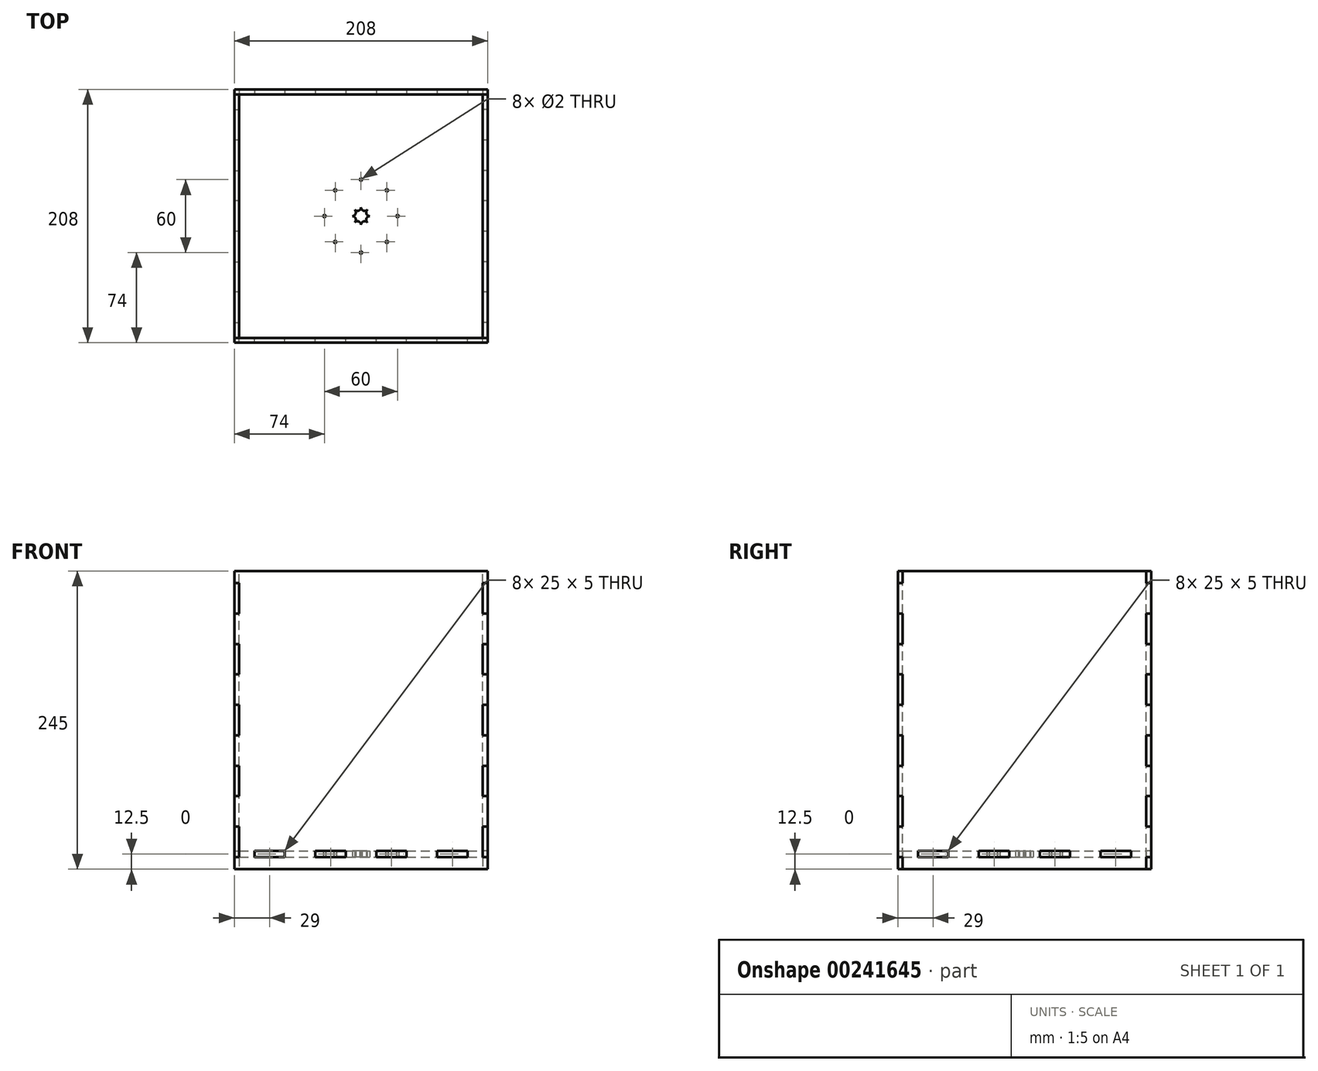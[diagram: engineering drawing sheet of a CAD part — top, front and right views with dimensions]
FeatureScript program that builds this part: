
annotation { "Feature Type Name" : "Feature", "Feature Type Description" : "" }
export const myFeature = defineFeature(function(context is Context, id is Id, definition is map)
    precondition{}
    {
        {
            var Q0;
            Q0=qCreatedBy(makeId("Top.planeOp"),FACE);
            var sketch = newSketch(context, id + "F0", { "sketchPlane" : qUnion([Q0])});
            skLineSegment(sketch, "E0.left", {"start": v(-100, -100) * mm, "end": v(-100, -100) * mm});
            skPoint(sketch, "E0.middle", {"position": v(0, 0) * mm});
            skLineSegment(sketch, "E1", {"start": v(-30, 0) * mm, "end": v(-30, 0) * mm});
            skLineSegment(sketch, "E2", {"start": v(0, -30) * mm, "end": v(0, -30) * mm});
            skLineSegment(sketch, "E3", {"start": v(-20.5, -20.5) * mm, "end": v(-5.12, -5.12) * mm});
            skArc(sketch, "E4.filletArc", {"start": v(0, -7.24) * mm, "mid": v(-1.85, -4.47) * mm, "end": v(-5.12, -5.12) * mm});
            skArc(sketch, "E5.filletArc", {"start": v(-5.12, -5.12) * mm, "mid": v(-4.47, -1.85) * mm, "end": v(-7.24, 0) * mm});
            skLineSegment(sketch, "E6", {"start": v(-29, 0) * mm, "end": v(-7.24, 0) * mm});
            skLineSegment(sketch, "E7", {"start": v(-5.12, 5.12) * mm, "end": v(-20.5, 20.5) * mm});
            skArc(sketch, "E8.filletArc", {"start": v(-7.24, 0) * mm, "mid": v(-4.47, 1.85) * mm, "end": v(-5.12, 5.12) * mm});
            skArc(sketch, "E9.filletArc", {"start": v(-5.12, 5.12) * mm, "mid": v(-1.85, 4.47) * mm, "end": v(0, 7.24) * mm});
            skLineSegment(sketch, "E10", {"start": v(7.24, 0) * mm, "end": v(29, 0) * mm});
            skLineSegment(sketch, "E11", {"start": v(0, -29) * mm, "end": v(0, -7.24) * mm});
            skLineSegment(sketch, "E12", {"start": v(0, 7.24) * mm, "end": v(0, 29) * mm});
            skLineSegment(sketch, "E13", {"start": v(0, 30) * mm, "end": v(0, 30) * mm});
            skLineSegment(sketch, "E14", {"start": v(30, 0) * mm, "end": v(30, 0) * mm});
            skLineSegment(sketch, "E15.trimOffspring", {"start": v(5.12, 5.12) * mm, "end": v(20.5, 20.5) * mm});
            skArc(sketch, "E16.filletArc", {"start": v(0, 7.24) * mm, "mid": v(1.85, 4.47) * mm, "end": v(5.12, 5.12) * mm});
            skArc(sketch, "E17.filletArc", {"start": v(5.12, 5.12) * mm, "mid": v(4.47, 1.85) * mm, "end": v(7.24, 0) * mm});
            skLineSegment(sketch, "E18.trimOffspring", {"start": v(5.12, -5.12) * mm, "end": v(20.5, -20.5) * mm});
            skArc(sketch, "E19.filletArc", {"start": v(5.12, -5.12) * mm, "mid": v(1.85, -4.47) * mm, "end": v(0, -7.24) * mm});
            skArc(sketch, "E20.filletArc", {"start": v(7.24, 0) * mm, "mid": v(4.47, -1.85) * mm, "end": v(5.12, -5.12) * mm});
            skCircle(sketch, "E21", {"center": v(-21.21, 21.21) * mm, "radius": 1 * mm});
            skCircle(sketch, "E22", {"center": v(-30, 0) * mm, "radius": 1 * mm});
            skCircle(sketch, "E23", {"center": v(-21.21, -21.21) * mm, "radius": 1 * mm});
            skCircle(sketch, "E24", {"center": v(0, -30) * mm, "radius": 1 * mm});
            skCircle(sketch, "E25", {"center": v(21.21, -21.21) * mm, "radius": 1 * mm});
            skCircle(sketch, "E26", {"center": v(30, 0) * mm, "radius": 1 * mm});
            skCircle(sketch, "E27", {"center": v(21.21, 21.21) * mm, "radius": 1 * mm});
            skCircle(sketch, "E28", {"center": v(0, 30) * mm, "radius": 1 * mm});
            skLineSegment(sketch, "E29", {"start": v(-100, -100) * mm, "end": v(-100, -87.5) * mm});
            skLineSegment(sketch, "E30", {"start": v(-100, 0) * mm, "end": v(-100, 12.5) * mm});
            skLineSegment(sketch, "E31", {"start": v(-100, 50) * mm, "end": v(-100, 62.5) * mm});
            skLineSegment(sketch, "E32", {"start": v(-100, -50) * mm, "end": v(-100, -37.5) * mm});
            skLineSegment(sketch, "E33", {"start": v(-100, -62.5) * mm, "end": v(-100, -50) * mm});
            skLineSegment(sketch, "E34", {"start": v(-100, -12.5) * mm, "end": v(-100, 0) * mm});
            skLineSegment(sketch, "E35", {"start": v(-100, 37.5) * mm, "end": v(-100, 50) * mm});
            skLineSegment(sketch, "E36", {"start": v(-100, 87.5) * mm, "end": v(-100, 100) * mm});
            skLineSegment(sketch, "E37", {"start": v(-100, 12.5) * mm, "end": v(-104, 12.5) * mm});
            skLineSegment(sketch, "E38", {"start": v(-104, 12.5) * mm, "end": v(-104, 37.5) * mm});
            skLineSegment(sketch, "E39", {"start": v(-104, 37.5) * mm, "end": v(-100, 37.5) * mm});
            skLineSegment(sketch, "E40", {"start": v(-100, -12.5) * mm, "end": v(-104, -12.5) * mm});
            skLineSegment(sketch, "E41", {"start": v(-104, -12.5) * mm, "end": v(-104, -37.5) * mm});
            skLineSegment(sketch, "E42", {"start": v(-104, -37.5) * mm, "end": v(-100, -37.5) * mm});
            skLineSegment(sketch, "E43", {"start": v(-100, -62.5) * mm, "end": v(-104, -62.5) * mm});
            skLineSegment(sketch, "E44", {"start": v(-104, -62.5) * mm, "end": v(-104, -87.5) * mm});
            skLineSegment(sketch, "E45", {"start": v(-104, -87.5) * mm, "end": v(-100, -87.5) * mm});
            skLineSegment(sketch, "E46", {"start": v(-100, 62.5) * mm, "end": v(-104, 62.5) * mm});
            skLineSegment(sketch, "E47", {"start": v(-104, 62.5) * mm, "end": v(-104, 87.5) * mm});
            skLineSegment(sketch, "E48", {"start": v(-104, 87.5) * mm, "end": v(-100, 87.5) * mm});
            skLineSegment(sketch, "E49.MirrorCS", {"start": v(100, -62.5) * mm, "end": v(104, -62.5) * mm});
            skLineSegment(sketch, "E50.MirrorCS", {"start": v(104, -87.5) * mm, "end": v(100, -87.5) * mm});
            skLineSegment(sketch, "E51.MirrorCS", {"start": v(104, -37.5) * mm, "end": v(100, -37.5) * mm});
            skLineSegment(sketch, "E52.MirrorCS", {"start": v(104, -62.5) * mm, "end": v(104, -87.5) * mm});
            skLineSegment(sketch, "E53.MirrorCS", {"start": v(104, -12.5) * mm, "end": v(104, -37.5) * mm});
            skLineSegment(sketch, "E54.MirrorCS", {"start": v(100, -100) * mm, "end": v(100, -87.5) * mm});
            skLineSegment(sketch, "E55.MirrorCS", {"start": v(100, -50) * mm, "end": v(100, -37.5) * mm});
            skLineSegment(sketch, "E56.MirrorCS", {"start": v(100, -62.5) * mm, "end": v(100, -50) * mm});
            skLineSegment(sketch, "E57.MirrorCS", {"start": v(100, -12.5) * mm, "end": v(104, -12.5) * mm});
            skLineSegment(sketch, "E58.MirrorCS", {"start": v(100, 12.5) * mm, "end": v(104, 12.5) * mm});
            skLineSegment(sketch, "E59.MirrorCS", {"start": v(104, 37.5) * mm, "end": v(100, 37.5) * mm});
            skLineSegment(sketch, "E60.MirrorCS", {"start": v(100, 62.5) * mm, "end": v(104, 62.5) * mm});
            skLineSegment(sketch, "E61.MirrorCS", {"start": v(104, 87.5) * mm, "end": v(100, 87.5) * mm});
            skLineSegment(sketch, "E62.MirrorCS", {"start": v(100, 87.5) * mm, "end": v(100, 100) * mm});
            skLineSegment(sketch, "E63.MirrorCS", {"start": v(100, 37.5) * mm, "end": v(100, 50) * mm});
            skLineSegment(sketch, "E64.MirrorCS", {"start": v(104, 12.5) * mm, "end": v(104, 37.5) * mm});
            skLineSegment(sketch, "E65.MirrorCS", {"start": v(100, -12.5) * mm, "end": v(100, 0) * mm});
            skLineSegment(sketch, "E66.MirrorCS", {"start": v(104, 62.5) * mm, "end": v(104, 87.5) * mm});
            skLineSegment(sketch, "E67.MirrorCS", {"start": v(100, 0) * mm, "end": v(100, 12.5) * mm});
            skLineSegment(sketch, "E68.MirrorCS", {"start": v(100, 50) * mm, "end": v(100, 62.5) * mm});
            skLineSegment(sketch, "E69.MirrorCS", {"start": v(-62.5, -100) * mm, "end": v(-62.5, -104) * mm});
            skLineSegment(sketch, "E70.MirrorCS", {"start": v(-87.5, -104) * mm, "end": v(-87.5, -100) * mm});
            skLineSegment(sketch, "E71.MirrorCS", {"start": v(-12.5, -100) * mm, "end": v(-12.5, -104) * mm});
            skLineSegment(sketch, "E72.MirrorCS", {"start": v(12.5, -100) * mm, "end": v(12.5, -104) * mm});
            skLineSegment(sketch, "E73.MirrorCS", {"start": v(62.5, -100) * mm, "end": v(62.5, -104) * mm});
            skLineSegment(sketch, "E74.MirrorCS", {"start": v(37.5, -104) * mm, "end": v(37.5, -100) * mm});
            skLineSegment(sketch, "E75.MirrorCS", {"start": v(-37.5, -104) * mm, "end": v(-37.5, -100) * mm});
            skLineSegment(sketch, "E76.MirrorCS", {"start": v(87.5, -104) * mm, "end": v(87.5, -100) * mm});
            skLineSegment(sketch, "E77.MirrorCS", {"start": v(-62.5, -104) * mm, "end": v(-87.5, -104) * mm});
            skLineSegment(sketch, "E78.MirrorCS", {"start": v(87.5, -100) * mm, "end": v(100, -100) * mm});
            skLineSegment(sketch, "E79.MirrorCS", {"start": v(37.5, -100) * mm, "end": v(50, -100) * mm});
            skLineSegment(sketch, "E80.MirrorCS", {"start": v(-50, -100) * mm, "end": v(-37.5, -100) * mm});
            skLineSegment(sketch, "E81.MirrorCS", {"start": v(-62.5, -100) * mm, "end": v(-50, -100) * mm});
            skLineSegment(sketch, "E82.MirrorCS", {"start": v(-100, -100) * mm, "end": v(-87.5, -100) * mm});
            skLineSegment(sketch, "E83.MirrorCS", {"start": v(12.5, -104) * mm, "end": v(37.5, -104) * mm});
            skLineSegment(sketch, "E84.MirrorCS", {"start": v(0, -100) * mm, "end": v(12.5, -100) * mm});
            skLineSegment(sketch, "E85.MirrorCS", {"start": v(50, -100) * mm, "end": v(62.5, -100) * mm});
            skLineSegment(sketch, "E86.MirrorCS", {"start": v(-12.5, -104) * mm, "end": v(-37.5, -104) * mm});
            skLineSegment(sketch, "E87.MirrorCS", {"start": v(-12.5, -100) * mm, "end": v(0, -100) * mm});
            skLineSegment(sketch, "E88.MirrorCS", {"start": v(62.5, -104) * mm, "end": v(87.5, -104) * mm});
            skLineSegment(sketch, "E89.MirrorCS", {"start": v(62.5, 100) * mm, "end": v(62.5, 104) * mm});
            skLineSegment(sketch, "E90.MirrorCS", {"start": v(37.5, 104) * mm, "end": v(37.5, 100) * mm});
            skLineSegment(sketch, "E91.MirrorCS", {"start": v(-37.5, 104) * mm, "end": v(-37.5, 100) * mm});
            skLineSegment(sketch, "E92.MirrorCS", {"start": v(87.5, 104) * mm, "end": v(87.5, 100) * mm});
            skLineSegment(sketch, "E93.MirrorCS", {"start": v(-12.5, 100) * mm, "end": v(-12.5, 104) * mm});
            skLineSegment(sketch, "E94.MirrorCS", {"start": v(-87.5, 104) * mm, "end": v(-87.5, 100) * mm});
            skLineSegment(sketch, "E95.MirrorCS", {"start": v(-62.5, 100) * mm, "end": v(-62.5, 104) * mm});
            skLineSegment(sketch, "E96.MirrorCS", {"start": v(12.5, 100) * mm, "end": v(12.5, 104) * mm});
            skLineSegment(sketch, "E97.MirrorCS", {"start": v(-12.5, 104) * mm, "end": v(-37.5, 104) * mm});
            skLineSegment(sketch, "E98.MirrorCS", {"start": v(-62.5, 104) * mm, "end": v(-87.5, 104) * mm});
            skLineSegment(sketch, "E99.MirrorCS", {"start": v(50, 100) * mm, "end": v(62.5, 100) * mm});
            skLineSegment(sketch, "E100.MirrorCS", {"start": v(-100, 100) * mm, "end": v(-87.5, 100) * mm});
            skLineSegment(sketch, "E101.MirrorCS", {"start": v(0, 100) * mm, "end": v(12.5, 100) * mm});
            skLineSegment(sketch, "E102.MirrorCS", {"start": v(12.5, 104) * mm, "end": v(37.5, 104) * mm});
            skLineSegment(sketch, "E103.MirrorCS", {"start": v(37.5, 100) * mm, "end": v(50, 100) * mm});
            skLineSegment(sketch, "E104.MirrorCS", {"start": v(62.5, 104) * mm, "end": v(87.5, 104) * mm});
            skLineSegment(sketch, "E105.MirrorCS", {"start": v(-12.5, 100) * mm, "end": v(0, 100) * mm});
            skLineSegment(sketch, "E106.MirrorCS", {"start": v(-50, 100) * mm, "end": v(-37.5, 100) * mm});
            skLineSegment(sketch, "E107.MirrorCS", {"start": v(87.5, 100) * mm, "end": v(100, 100) * mm});
            skLineSegment(sketch, "E108.MirrorCS", {"start": v(-62.5, 100) * mm, "end": v(-50, 100) * mm});
            skSolve(sketch);
        }
        {
            var Q0;
            Q0 = qSketchRegion(id + "F0", true);
            extrude(context, id + "F1", {"entities" : qUnion([Q0]), "depth" : 5 * mm});
        }
        {
            var Q0;
            Q0=makeQuery(id+"F1.opExtrude","SWEPT_FACE",FACE,{"disambiguationData":[OSD([sQuery(id+"F0.wireOp",EDGE,"E80.MirrorCS"),sQuery(id+"F0.wireOp",EDGE,"E81.MirrorCS")])]});
            var sketch = newSketch(context, id + "F2", { "sketchPlane" : qUnion([Q0])});
            skLineSegment(sketch, "E109", {"start": v(-104, -10) * mm, "end": v(104, -10) * mm});
            skLineSegment(sketch, "E110", {"start": v(-87.5, 0) * mm, "end": v(-87.5, 5) * mm});
            skLineSegment(sketch, "E111", {"start": v(-87.5, 5) * mm, "end": v(-62.5, 5) * mm});
            skLineSegment(sketch, "E112", {"start": v(-62.5, 5) * mm, "end": v(-62.5, 0) * mm});
            skLineSegment(sketch, "E113", {"start": v(-62.5, 0) * mm, "end": v(-87.5, 0) * mm});
            skLineSegment(sketch, "E114.1.0.0", {"start": v(-37.5, 5) * mm, "end": v(-12.5, 5) * mm});
            skLineSegment(sketch, "E114.1.0.1", {"start": v(-12.5, 0) * mm, "end": v(-37.5, 0) * mm});
            skLineSegment(sketch, "E114.1.0.2", {"start": v(-12.5, 5) * mm, "end": v(-12.5, 0) * mm});
            skLineSegment(sketch, "E114.1.0.3", {"start": v(-37.5, 0) * mm, "end": v(-37.5, 5) * mm});
            skLineSegment(sketch, "E114.2.0.0", {"start": v(12.5, 5) * mm, "end": v(37.5, 5) * mm});
            skLineSegment(sketch, "E114.2.0.1", {"start": v(37.5, 0) * mm, "end": v(12.5, 0) * mm});
            skLineSegment(sketch, "E114.2.0.2", {"start": v(37.5, 5) * mm, "end": v(37.5, 0) * mm});
            skLineSegment(sketch, "E114.2.0.3", {"start": v(12.5, 0) * mm, "end": v(12.5, 5) * mm});
            skLineSegment(sketch, "E114.3.0.0", {"start": v(62.5, 5) * mm, "end": v(87.5, 5) * mm});
            skLineSegment(sketch, "E114.3.0.1", {"start": v(87.5, 0) * mm, "end": v(62.5, 0) * mm});
            skLineSegment(sketch, "E114.3.0.2", {"start": v(87.5, 5) * mm, "end": v(87.5, 0) * mm});
            skLineSegment(sketch, "E114.3.0.3", {"start": v(62.5, 0) * mm, "end": v(62.5, 5) * mm});
            skLineSegment(sketch, "E115.0", {"start": v(-104, 235) * mm, "end": v(104, 235) * mm});
            skLineSegment(sketch, "E116", {"start": v(-104, 0) * mm, "end": v(-104, -10) * mm});
            skLineSegment(sketch, "E117", {"start": v(-104, 0) * mm, "end": v(-100, 0) * mm});
            skLineSegment(sketch, "E118", {"start": v(-100, 0) * mm, "end": v(-100, 25) * mm});
            skLineSegment(sketch, "E119", {"start": v(-100, 25) * mm, "end": v(-104, 25) * mm});
            skLineSegment(sketch, "E120.0.1.0", {"start": v(-104, 50) * mm, "end": v(-100, 50) * mm});
            skLineSegment(sketch, "E120.0.1.1", {"start": v(-100, 50) * mm, "end": v(-100, 75) * mm});
            skLineSegment(sketch, "E120.0.1.2", {"start": v(-100, 75) * mm, "end": v(-104, 75) * mm});
            skLineSegment(sketch, "E120.0.2.0", {"start": v(-104, 100) * mm, "end": v(-100, 100) * mm});
            skLineSegment(sketch, "E120.0.2.1", {"start": v(-100, 100) * mm, "end": v(-100, 125) * mm});
            skLineSegment(sketch, "E120.0.2.2", {"start": v(-100, 125) * mm, "end": v(-104, 125) * mm});
            skLineSegment(sketch, "E120.0.3.0", {"start": v(-104, 150) * mm, "end": v(-100, 150) * mm});
            skLineSegment(sketch, "E120.0.3.1", {"start": v(-100, 150) * mm, "end": v(-100, 175) * mm});
            skLineSegment(sketch, "E120.0.3.2", {"start": v(-100, 175) * mm, "end": v(-104, 175) * mm});
            skLineSegment(sketch, "E120.0.4.0", {"start": v(-104, 200) * mm, "end": v(-100, 200) * mm});
            skLineSegment(sketch, "E120.0.4.1", {"start": v(-100, 200) * mm, "end": v(-100, 225) * mm});
            skLineSegment(sketch, "E120.0.4.2", {"start": v(-100, 225) * mm, "end": v(-104, 225) * mm});
            skLineSegment(sketch, "E121", {"start": v(-104, 235) * mm, "end": v(-104, 225) * mm});
            skLineSegment(sketch, "E122", {"start": v(-104, 200) * mm, "end": v(-104, 175) * mm});
            skLineSegment(sketch, "E123", {"start": v(-104, 150) * mm, "end": v(-104, 125) * mm});
            skLineSegment(sketch, "E124", {"start": v(-104, 100) * mm, "end": v(-104, 75) * mm});
            skLineSegment(sketch, "E125", {"start": v(-104, 50) * mm, "end": v(-104, 25) * mm});
            skLineSegment(sketch, "E126.MirrorCS", {"start": v(104, 235) * mm, "end": v(104, 225) * mm});
            skLineSegment(sketch, "E127.MirrorCS", {"start": v(104, 100) * mm, "end": v(100, 100) * mm});
            skLineSegment(sketch, "E128.MirrorCS", {"start": v(100, 25) * mm, "end": v(104, 25) * mm});
            skLineSegment(sketch, "E129.MirrorCS", {"start": v(104, 150) * mm, "end": v(100, 150) * mm});
            skLineSegment(sketch, "E130.MirrorCS", {"start": v(104, 0) * mm, "end": v(100, 0) * mm});
            skLineSegment(sketch, "E131.MirrorCS", {"start": v(104, 0) * mm, "end": v(104, -10) * mm});
            skLineSegment(sketch, "E132.MirrorCS", {"start": v(104, 50) * mm, "end": v(100, 50) * mm});
            skLineSegment(sketch, "E133.MirrorCS", {"start": v(104, 200) * mm, "end": v(100, 200) * mm});
            skLineSegment(sketch, "E134.MirrorCS", {"start": v(100, 75) * mm, "end": v(104, 75) * mm});
            skLineSegment(sketch, "E135.MirrorCS", {"start": v(100, 225) * mm, "end": v(104, 225) * mm});
            skLineSegment(sketch, "E136.MirrorCS", {"start": v(100, 175) * mm, "end": v(104, 175) * mm});
            skLineSegment(sketch, "E137.MirrorCS", {"start": v(100, 125) * mm, "end": v(104, 125) * mm});
            skLineSegment(sketch, "E138.MirrorCS", {"start": v(104, 100) * mm, "end": v(104, 75) * mm});
            skLineSegment(sketch, "E139.MirrorCS", {"start": v(100, 50) * mm, "end": v(100, 75) * mm});
            skLineSegment(sketch, "E140.MirrorCS", {"start": v(104, 50) * mm, "end": v(104, 25) * mm});
            skLineSegment(sketch, "E141.MirrorCS", {"start": v(100, 150) * mm, "end": v(100, 175) * mm});
            skLineSegment(sketch, "E142.MirrorCS", {"start": v(100, 0) * mm, "end": v(100, 25) * mm});
            skLineSegment(sketch, "E143.MirrorCS", {"start": v(100, 200) * mm, "end": v(100, 225) * mm});
            skLineSegment(sketch, "E144.MirrorCS", {"start": v(104, 150) * mm, "end": v(104, 125) * mm});
            skLineSegment(sketch, "E145.MirrorCS", {"start": v(100, 100) * mm, "end": v(100, 125) * mm});
            skLineSegment(sketch, "E146.MirrorCS", {"start": v(104, 200) * mm, "end": v(104, 175) * mm});
            skSolve(sketch);
        }
        {
            var Q0;
            Q0 = qSketchRegion(id + "F2", true);
            extrude(context, id + "F3", {"entities" : qUnion([Q0]), "depth" : 4 * mm});
        }
        {
            var Q0;
            Q0=makeQuery(id+"F3.opExtrude","SWEPT_FACE",FACE,{"disambiguationData":[OSD([sQuery(id+"F2.wireOp",EDGE,"E142.MirrorCS")])]});
            var sketch = newSketch(context, id + "F4", { "sketchPlane" : qUnion([Q0])});
            skLineSegment(sketch, "E147", {"start": v(-104, 0) * mm, "end": v(-100, 0) * mm});
            skLineSegment(sketch, "E148", {"start": v(-100, 0) * mm, "end": v(-100, -10) * mm});
            skLineSegment(sketch, "E149", {"start": v(-104, 0) * mm, "end": v(-104, 25) * mm});
            skLineSegment(sketch, "E150", {"start": v(-104, 25) * mm, "end": v(-100, 25) * mm});
            skLineSegment(sketch, "E151.0.1.0", {"start": v(-104, 50) * mm, "end": v(-104, 75) * mm});
            skLineSegment(sketch, "E151.0.1.1", {"start": v(-104, 75) * mm, "end": v(-100, 75) * mm});
            skLineSegment(sketch, "E151.0.1.2", {"start": v(-104, 50) * mm, "end": v(-100, 50) * mm});
            skLineSegment(sketch, "E151.0.2.0", {"start": v(-104, 100) * mm, "end": v(-104, 125) * mm});
            skLineSegment(sketch, "E151.0.2.1", {"start": v(-104, 125) * mm, "end": v(-100, 125) * mm});
            skLineSegment(sketch, "E151.0.2.2", {"start": v(-104, 100) * mm, "end": v(-100, 100) * mm});
            skLineSegment(sketch, "E151.0.3.0", {"start": v(-104, 150) * mm, "end": v(-104, 175) * mm});
            skLineSegment(sketch, "E151.0.3.1", {"start": v(-104, 175) * mm, "end": v(-100, 175) * mm});
            skLineSegment(sketch, "E151.0.3.2", {"start": v(-104, 150) * mm, "end": v(-100, 150) * mm});
            skLineSegment(sketch, "E151.0.4.0", {"start": v(-104, 200) * mm, "end": v(-104, 225) * mm});
            skLineSegment(sketch, "E151.0.4.1", {"start": v(-104, 225) * mm, "end": v(-100, 225) * mm});
            skLineSegment(sketch, "E151.0.4.2", {"start": v(-104, 200) * mm, "end": v(-100, 200) * mm});
            skLineSegment(sketch, "E152", {"start": v(-100, 25) * mm, "end": v(-100, 50) * mm});
            skLineSegment(sketch, "E153", {"start": v(-100, 75) * mm, "end": v(-100, 100) * mm});
            skLineSegment(sketch, "E154", {"start": v(-100, 125) * mm, "end": v(-100, 150) * mm});
            skLineSegment(sketch, "E155", {"start": v(-100, 175) * mm, "end": v(-100, 200) * mm});
            skLineSegment(sketch, "E156", {"start": v(-100, 225) * mm, "end": v(-100, 235) * mm});
            skLineSegment(sketch, "E157.MirrorCS", {"start": v(104, 225) * mm, "end": v(100, 225) * mm});
            skLineSegment(sketch, "E158.MirrorCS", {"start": v(104, 200) * mm, "end": v(100, 200) * mm});
            skLineSegment(sketch, "E159.MirrorCS", {"start": v(104, 0) * mm, "end": v(100, 0) * mm});
            skLineSegment(sketch, "E160.MirrorCS", {"start": v(104, 25) * mm, "end": v(100, 25) * mm});
            skLineSegment(sketch, "E161.MirrorCS", {"start": v(104, 75) * mm, "end": v(100, 75) * mm});
            skLineSegment(sketch, "E162.MirrorCS", {"start": v(104, 50) * mm, "end": v(100, 50) * mm});
            skLineSegment(sketch, "E163.MirrorCS", {"start": v(104, 125) * mm, "end": v(100, 125) * mm});
            skLineSegment(sketch, "E164.MirrorCS", {"start": v(104, 100) * mm, "end": v(100, 100) * mm});
            skLineSegment(sketch, "E165.MirrorCS", {"start": v(104, 150) * mm, "end": v(100, 150) * mm});
            skLineSegment(sketch, "E166.MirrorCS", {"start": v(104, 175) * mm, "end": v(100, 175) * mm});
            skLineSegment(sketch, "E167.MirrorCS", {"start": v(100, 0) * mm, "end": v(100, -10) * mm});
            skLineSegment(sketch, "E168.MirrorCS", {"start": v(100, 225) * mm, "end": v(100, 235) * mm});
            skLineSegment(sketch, "E169.MirrorCS", {"start": v(100, 75) * mm, "end": v(100, 100) * mm});
            skLineSegment(sketch, "E170.MirrorCS", {"start": v(100, 125) * mm, "end": v(100, 150) * mm});
            skLineSegment(sketch, "E171.MirrorCS", {"start": v(104, 200) * mm, "end": v(104, 225) * mm});
            skLineSegment(sketch, "E172.MirrorCS", {"start": v(100, 25) * mm, "end": v(100, 50) * mm});
            skLineSegment(sketch, "E173.MirrorCS", {"start": v(104, 0) * mm, "end": v(104, 25) * mm});
            skLineSegment(sketch, "E174.MirrorCS", {"start": v(104, 50) * mm, "end": v(104, 75) * mm});
            skLineSegment(sketch, "E175.MirrorCS", {"start": v(104, 100) * mm, "end": v(104, 125) * mm});
            skLineSegment(sketch, "E176.MirrorCS", {"start": v(100, 175) * mm, "end": v(100, 200) * mm});
            skLineSegment(sketch, "E177.MirrorCS", {"start": v(104, 150) * mm, "end": v(104, 175) * mm});
            skLineSegment(sketch, "E178", {"start": v(-87.5, 0) * mm, "end": v(-87.5, 5) * mm});
            skLineSegment(sketch, "E179", {"start": v(-87.5, 5) * mm, "end": v(-62.5, 5) * mm});
            skLineSegment(sketch, "E180", {"start": v(-62.5, 5) * mm, "end": v(-62.5, 0) * mm});
            skLineSegment(sketch, "E181", {"start": v(-62.5, 0) * mm, "end": v(-87.5, 0) * mm});
            skLineSegment(sketch, "E182", {"start": v(-100, 235) * mm, "end": v(100, 235) * mm});
            skLineSegment(sketch, "E183", {"start": v(100, -10) * mm, "end": v(-100, -10) * mm});
            skLineSegment(sketch, "E184.1.0.0", {"start": v(-37.5, 0) * mm, "end": v(-37.5, 5) * mm});
            skLineSegment(sketch, "E184.1.0.1", {"start": v(-12.5, 5) * mm, "end": v(-12.5, 0) * mm});
            skLineSegment(sketch, "E184.1.0.2", {"start": v(-37.5, 5) * mm, "end": v(-12.5, 5) * mm});
            skLineSegment(sketch, "E184.1.0.3", {"start": v(-12.5, 0) * mm, "end": v(-37.5, 0) * mm});
            skLineSegment(sketch, "E184.2.0.0", {"start": v(12.5, 0) * mm, "end": v(12.5, 5) * mm});
            skLineSegment(sketch, "E184.2.0.1", {"start": v(37.5, 5) * mm, "end": v(37.5, 0) * mm});
            skLineSegment(sketch, "E184.2.0.2", {"start": v(12.5, 5) * mm, "end": v(37.5, 5) * mm});
            skLineSegment(sketch, "E184.2.0.3", {"start": v(37.5, 0) * mm, "end": v(12.5, 0) * mm});
            skLineSegment(sketch, "E184.3.0.0", {"start": v(62.5, 0) * mm, "end": v(62.5, 5) * mm});
            skLineSegment(sketch, "E184.3.0.1", {"start": v(87.5, 5) * mm, "end": v(87.5, 0) * mm});
            skLineSegment(sketch, "E184.3.0.2", {"start": v(62.5, 5) * mm, "end": v(87.5, 5) * mm});
            skLineSegment(sketch, "E184.3.0.3", {"start": v(87.5, 0) * mm, "end": v(62.5, 0) * mm});
            skSolve(sketch);
        }
        {
            var Q0;
            Q0 = qSketchRegion(id + "F4", true);
            extrude(context, id + "F5", {"entities" : qUnion([Q0]), "depth" : 4 * mm});
        }
        {
            var Q0;
            Q0=makeQuery(id+"F3.opExtrude","SWEPT_BODY",BODY,{"disambiguationData":[OSD([sQuery(id+"F2.wireOp",EDGE,"E109"),sQuery(id+"F2.wireOp",EDGE,"E110"),sQuery(id+"F2.wireOp",EDGE,"E111"),sQuery(id+"F2.wireOp",EDGE,"E112"),sQuery(id+"F2.wireOp",EDGE,"E113"),sQuery(id+"F2.wireOp",EDGE,"E114.1.0.0"),sQuery(id+"F2.wireOp",EDGE,"E114.1.0.1"),sQuery(id+"F2.wireOp",EDGE,"E114.1.0.2"),sQuery(id+"F2.wireOp",EDGE,"E114.1.0.3"),sQuery(id+"F2.wireOp",EDGE,"E114.2.0.0"),sQuery(id+"F2.wireOp",EDGE,"E114.2.0.1"),sQuery(id+"F2.wireOp",EDGE,"E114.2.0.2"),sQuery(id+"F2.wireOp",EDGE,"E114.2.0.3"),sQuery(id+"F2.wireOp",EDGE,"E114.3.0.0"),sQuery(id+"F2.wireOp",EDGE,"E114.3.0.1"),sQuery(id+"F2.wireOp",EDGE,"E114.3.0.2"),sQuery(id+"F2.wireOp",EDGE,"E114.3.0.3"),sQuery(id+"F2.wireOp",EDGE,"E115.0"),sQuery(id+"F2.wireOp",EDGE,"E116"),sQuery(id+"F2.wireOp",EDGE,"E117"),sQuery(id+"F2.wireOp",EDGE,"E118"),sQuery(id+"F2.wireOp",EDGE,"E119"),sQuery(id+"F2.wireOp",EDGE,"E120.0.1.0"),sQuery(id+"F2.wireOp",EDGE,"E120.0.1.1"),sQuery(id+"F2.wireOp",EDGE,"E120.0.1.2"),sQuery(id+"F2.wireOp",EDGE,"E120.0.2.0"),sQuery(id+"F2.wireOp",EDGE,"E120.0.2.1"),sQuery(id+"F2.wireOp",EDGE,"E120.0.2.2"),sQuery(id+"F2.wireOp",EDGE,"E120.0.3.0"),sQuery(id+"F2.wireOp",EDGE,"E120.0.3.1"),sQuery(id+"F2.wireOp",EDGE,"E120.0.3.2"),sQuery(id+"F2.wireOp",EDGE,"E120.0.4.0"),sQuery(id+"F2.wireOp",EDGE,"E120.0.4.1"),sQuery(id+"F2.wireOp",EDGE,"E120.0.4.2"),sQuery(id+"F2.wireOp",EDGE,"E121"),sQuery(id+"F2.wireOp",EDGE,"E122"),sQuery(id+"F2.wireOp",EDGE,"E123"),sQuery(id+"F2.wireOp",EDGE,"E124"),sQuery(id+"F2.wireOp",EDGE,"E125"),sQuery(id+"F2.wireOp",EDGE,"E126.MirrorCS"),sQuery(id+"F2.wireOp",EDGE,"E127.MirrorCS"),sQuery(id+"F2.wireOp",EDGE,"E128.MirrorCS"),sQuery(id+"F2.wireOp",EDGE,"E129.MirrorCS"),sQuery(id+"F2.wireOp",EDGE,"E130.MirrorCS"),sQuery(id+"F2.wireOp",EDGE,"E131.MirrorCS"),sQuery(id+"F2.wireOp",EDGE,"E132.MirrorCS"),sQuery(id+"F2.wireOp",EDGE,"E133.MirrorCS"),sQuery(id+"F2.wireOp",EDGE,"E134.MirrorCS"),sQuery(id+"F2.wireOp",EDGE,"E135.MirrorCS"),sQuery(id+"F2.wireOp",EDGE,"E136.MirrorCS"),sQuery(id+"F2.wireOp",EDGE,"E137.MirrorCS"),sQuery(id+"F2.wireOp",EDGE,"E138.MirrorCS"),sQuery(id+"F2.wireOp",EDGE,"E139.MirrorCS"),sQuery(id+"F2.wireOp",EDGE,"E140.MirrorCS"),sQuery(id+"F2.wireOp",EDGE,"E141.MirrorCS"),sQuery(id+"F2.wireOp",EDGE,"E142.MirrorCS"),sQuery(id+"F2.wireOp",EDGE,"E143.MirrorCS"),sQuery(id+"F2.wireOp",EDGE,"E144.MirrorCS"),sQuery(id+"F2.wireOp",EDGE,"E145.MirrorCS"),sQuery(id+"F2.wireOp",EDGE,"E146.MirrorCS")])]});
            var Q1;
            Q1=qCreatedBy(makeId("Front.planeOp"),FACE);
            mirror(context, id + "F6", {"entities" : qUnion([Q0]), "mirrorPlane" : qUnion([Q1])});
        }
        {
            var Q0;
            Q0=makeQuery(id+"F5.opExtrude","SWEPT_BODY",BODY,{"disambiguationData":[OSD([sQuery(id+"F4.wireOp",EDGE,"E147"),sQuery(id+"F4.wireOp",EDGE,"E148"),sQuery(id+"F4.wireOp",EDGE,"E149"),sQuery(id+"F4.wireOp",EDGE,"E150"),sQuery(id+"F4.wireOp",EDGE,"E151.0.1.0"),sQuery(id+"F4.wireOp",EDGE,"E151.0.1.1"),sQuery(id+"F4.wireOp",EDGE,"E151.0.1.2"),sQuery(id+"F4.wireOp",EDGE,"E151.0.2.0"),sQuery(id+"F4.wireOp",EDGE,"E151.0.2.1"),sQuery(id+"F4.wireOp",EDGE,"E151.0.2.2"),sQuery(id+"F4.wireOp",EDGE,"E151.0.3.0"),sQuery(id+"F4.wireOp",EDGE,"E151.0.3.1"),sQuery(id+"F4.wireOp",EDGE,"E151.0.3.2"),sQuery(id+"F4.wireOp",EDGE,"E151.0.4.0"),sQuery(id+"F4.wireOp",EDGE,"E151.0.4.1"),sQuery(id+"F4.wireOp",EDGE,"E151.0.4.2"),sQuery(id+"F4.wireOp",EDGE,"E152"),sQuery(id+"F4.wireOp",EDGE,"E153"),sQuery(id+"F4.wireOp",EDGE,"E154"),sQuery(id+"F4.wireOp",EDGE,"E155"),sQuery(id+"F4.wireOp",EDGE,"E156"),sQuery(id+"F4.wireOp",EDGE,"E157.MirrorCS"),sQuery(id+"F4.wireOp",EDGE,"E158.MirrorCS"),sQuery(id+"F4.wireOp",EDGE,"E159.MirrorCS"),sQuery(id+"F4.wireOp",EDGE,"E160.MirrorCS"),sQuery(id+"F4.wireOp",EDGE,"E161.MirrorCS"),sQuery(id+"F4.wireOp",EDGE,"E162.MirrorCS"),sQuery(id+"F4.wireOp",EDGE,"E163.MirrorCS"),sQuery(id+"F4.wireOp",EDGE,"E164.MirrorCS"),sQuery(id+"F4.wireOp",EDGE,"E165.MirrorCS"),sQuery(id+"F4.wireOp",EDGE,"E166.MirrorCS"),sQuery(id+"F4.wireOp",EDGE,"E167.MirrorCS"),sQuery(id+"F4.wireOp",EDGE,"E168.MirrorCS"),sQuery(id+"F4.wireOp",EDGE,"E169.MirrorCS"),sQuery(id+"F4.wireOp",EDGE,"E170.MirrorCS"),sQuery(id+"F4.wireOp",EDGE,"E171.MirrorCS"),sQuery(id+"F4.wireOp",EDGE,"E172.MirrorCS"),sQuery(id+"F4.wireOp",EDGE,"E173.MirrorCS"),sQuery(id+"F4.wireOp",EDGE,"E174.MirrorCS"),sQuery(id+"F4.wireOp",EDGE,"E175.MirrorCS"),sQuery(id+"F4.wireOp",EDGE,"E176.MirrorCS"),sQuery(id+"F4.wireOp",EDGE,"E177.MirrorCS"),sQuery(id+"F4.wireOp",EDGE,"E178"),sQuery(id+"F4.wireOp",EDGE,"E179"),sQuery(id+"F4.wireOp",EDGE,"E180"),sQuery(id+"F4.wireOp",EDGE,"E181"),sQuery(id+"F4.wireOp",EDGE,"E182"),sQuery(id+"F4.wireOp",EDGE,"E183"),sQuery(id+"F4.wireOp",EDGE,"E184.1.0.0"),sQuery(id+"F4.wireOp",EDGE,"E184.1.0.1"),sQuery(id+"F4.wireOp",EDGE,"E184.1.0.2"),sQuery(id+"F4.wireOp",EDGE,"E184.1.0.3"),sQuery(id+"F4.wireOp",EDGE,"E184.2.0.0"),sQuery(id+"F4.wireOp",EDGE,"E184.2.0.1"),sQuery(id+"F4.wireOp",EDGE,"E184.2.0.2"),sQuery(id+"F4.wireOp",EDGE,"E184.2.0.3"),sQuery(id+"F4.wireOp",EDGE,"E184.3.0.0"),sQuery(id+"F4.wireOp",EDGE,"E184.3.0.1"),sQuery(id+"F4.wireOp",EDGE,"E184.3.0.2"),sQuery(id+"F4.wireOp",EDGE,"E184.3.0.3")])]});
            var Q1;
            Q1=qCreatedBy(makeId("Right.planeOp"),FACE);
            mirror(context, id + "F7", {"entities" : qUnion([Q0]), "mirrorPlane" : qUnion([Q1])});
        }
    });
